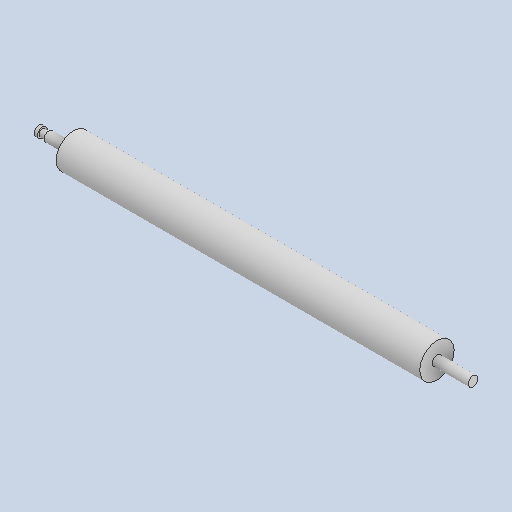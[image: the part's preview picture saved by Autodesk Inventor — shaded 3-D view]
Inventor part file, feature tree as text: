
AUTODESK INVENTOR PART (.ipt)
format: ipt  version: 2023 (Build 270158000, 158)  size: 104,960 bytes
history: native  units: in
note: dims shown in document units (in); Inventor stores cm internally (conversion verified against a paired STEP export)
features: extrude x5, sketch x5
ambient origin geometry x8: Origin, YZ Plane, XZ Plane, XY Plane, X Axis, Y Axis, Z Axis, Center Point
bodies: Solid1 (feature_tree)
feature tree (10):
  extrude  "Extrusion1"  Depth=8.7402in TaperAngle=0.0deg
  extrude  "Extrusion2"  Depth=0.8661in TaperAngle=0.0deg
  extrude  "Extrusion3"  Depth=0.5906in TaperAngle=0.0deg
  extrude  "Extrusion4"  Depth=0.1575in TaperAngle=0.0deg
  extrude  "Extrusion5"  Depth=0.0787in TaperAngle=0.0deg
  sketch  "Sketch1"  dims[d0=0.8268in d1=8.7402in d2=0.0in]
  sketch  "Sketch2"  dims[d3=0.2362in d4=0.8661in d5=0.0in]
  sketch  "Sketch3"  dims[d6=0.2362in d7=0.5906in d8=0.0in]
  sketch  "Sketch4"  dims[d9=0.1575in d10=0.1575in d11=0.0in]
  sketch  "Sketch5"  dims[d12=0.2362in d13=0.0787in d14=0.0in]
